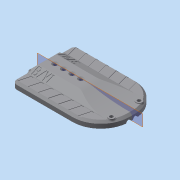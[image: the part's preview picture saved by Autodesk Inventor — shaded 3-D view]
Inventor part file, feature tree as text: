
AUTODESK INVENTOR PART (.ipt)
format: ipt  version: 2014 SP1 (Build 180222100, 222)  size: 615,936 bytes
history: native  units: in
note: dims shown in document units (in); Inventor stores cm internally (conversion verified against a paired STEP export)
features: extrude x12, sketch x10, fillet x6, chamfer x4, plane x2, other x1, pattern_linear x1, mirror x1
ambient origin geometry x8: Origin, YZ Plane, XZ Plane, XY Plane, X Axis, Y Axis, Z Axis, Center Point
bodies: Solid1 (feature_tree)
feature tree (37):
  other  "electronicsbox_top.ipt"
  plane  "Work Plane1"
  extrude  "Extrusion1"  Depth=0.25in TaperAngle=0.0deg
  sketch  "Sketch7"  dims[d0=0.3937in d9=0.25in d10=0.0in]
  extrude  "Extrusion8"  Depth=0.2756in
  extrude  "Extrusion11"  Depth=0.1969in
  extrude  "Extrusion18"  Depth=1.0in TaperAngle=0.0deg
  fillet  "Fillet6"  Radius=0.75in
  fillet  "Fillet7"  Radius=0.5in
  extrude  "Extrusion23"  Depth=1.0in
  extrude  "Extrusion24"  Depth=0.125in TaperAngle=0.0deg
  extrude  "Extrusion25"  Depth=1.0in
  chamfer  "Chamfer14"  Distance=0.25in
  extrude  "Extrusion26"  Depth=1.5748in
  extrude  "Extrusion28"  Depth=0.0625in TaperAngle=45.0deg
  chamfer  "Chamfer18"  Distance=0.315in
  chamfer  "Chamfer19"  Distance=0.315in
  fillet  "Fillet12"  Radius=0.315in
  chamfer  "Chamfer20"  Distance=0.315in
  fillet  "Fillet13"  Radius=0.125in
  extrude  "Extrusion29"  Depth=0.375in
  pattern_linear  "Rectangular Pattern1"  Spacing1=0.375in  [1 undecoded]
  plane  "Work Plane2"
  mirror  "Mirror1"
  extrude  "Extrusion30"  Depth=0.0312in TaperAngle=0.0deg
  extrude  "Extrusion31"  Depth=0.125in TaperAngle=45.0deg
  fillet  "Fillet14"  Radius=0.25in
  fillet  "Fillet15"  Radius=10.0in
  sketch  "Sketch18"  dims[d53=0.125in d54=0.0in d68=0.2756in]
  sketch  "Sketch23"  dims[d69=0.2756in d70=0.1969in]
  sketch  "Sketch24"  dims[d71=0.1969in d72=1.0in d73=0.0in d111=0.75in d112=0.5in d113=0.0in]
  sketch  "Sketch25"  dims[d128=0.0312in d150=1.0in]
  sketch  "Sketch26"  dims[d151=0.5in d152=0.125in d153=0.0in]
  sketch  "Sketch28"  dims[d154=2.5in d155=1.0in]
  sketch  "Sketch29"  dims[d156=1.0in d157=0.25in d158=0.0in]
  sketch  "Sketch30"  dims[d164=0.1988in d165=1.5748in d167=0.5118in d168=0.3937in d170=1.0in]
  sketch  "Sketch31"  dims[d172=0.25in d173=0.0in d174=0.0625in d175=0.125in d176=45.0deg d177=0.315in d178=0.315in d179=0.315in d180=0.315in d181=0.125in d182=0.0in d193=0.375in d194=0.375in d195=0.0312in d196=0.0in d200=0.125in d201=0.125in d202=45.0deg d203=0.25in d204=0.125in d205=45.0deg d206=10.0in d207=0.325in d208=0.125in d209=45.0deg d210=2.0in d211=75.0deg d212=0.15in d213=0.25in d214=0.025in d215=0.0in d216=2.7559in d218=0.6in d219=0.0312in d220=0.0in d221=0.0312in d222=0.0in d223=0.125in d224=0.125in]
note: 1 required parameter value undecoded (feature->parameter linkage not recoverable at this tier; creation-order binding heuristic only, values carry confidence <= 0.55)
